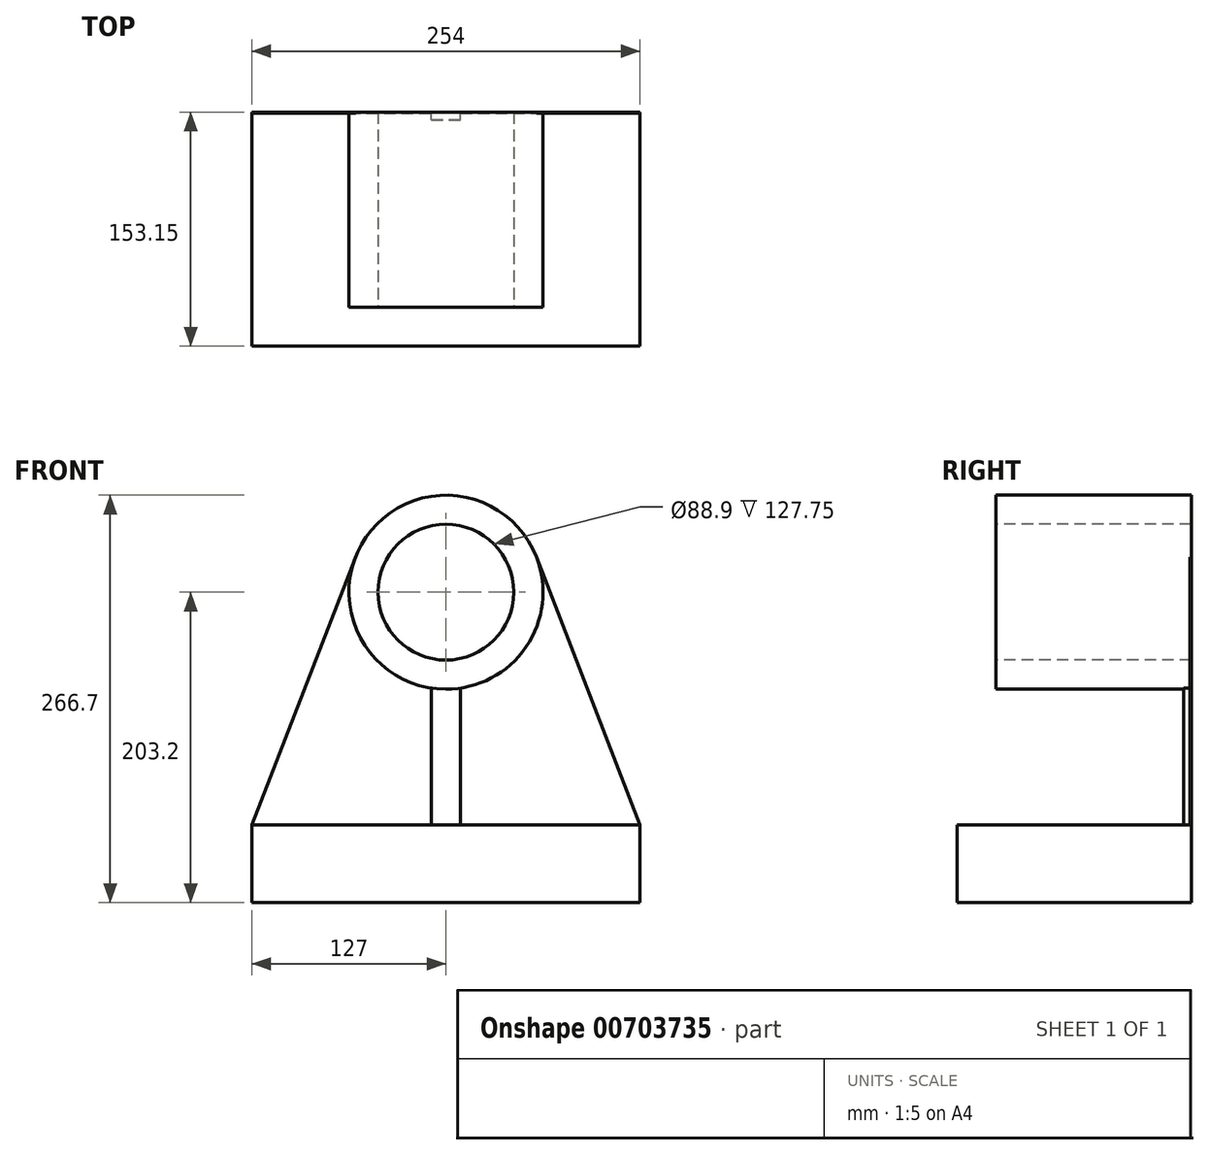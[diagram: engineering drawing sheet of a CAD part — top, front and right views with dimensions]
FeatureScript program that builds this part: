
annotation { "Feature Type Name" : "Feature", "Feature Type Description" : "" }
export const myFeature = defineFeature(function(context is Context, id is Id, definition is map)
    precondition{}
    {
        {
            assignVariable(context, id + "F0", {"name" : "C", "anyValue" : 0.75});
        }
        {
            var Q0;
            Q0=qCreatedBy(makeId("Front.planeOp"),FACE);
            var sketch = newSketch(context, id + "F1", { "sketchPlane" : qUnion([Q0])});
            skLineSegment(sketch, "E0.bottom", {"start": v(0, 0) * mm, "end": v(-254, 0) * mm});
            skLineSegment(sketch, "E0.left", {"start": v(0, 0) * mm, "end": v(0, 50.8) * mm});
            skLineSegment(sketch, "E0.right", {"start": v(-254, 0) * mm, "end": v(-254, 50.8) * mm});
            skLineSegment(sketch, "E1", {"start": v(0, 50.8) * mm, "end": v(-67.77, 226.1) * mm});
            skArc(sketch, "E2", {"start": v(-67.77, 226.1) * mm, "mid": v(-127, 266.7) * mm, "end": v(-186.23, 226.1) * mm});
            skLineSegment(sketch, "E3", {"start": v(-254, 50.8) * mm, "end": v(-186.23, 226.1) * mm});
            skLineSegment(sketch, "E4", {"start": v(-127, 203.2) * mm, "end": v(-127, 0) * mm, "construction": true});
            skSolve(sketch);
        }
        {
            var Q0;
            Q0 = qSketchRegion(id + "F1", true);
            extrude(context, id + "F2", {"entities" : qUnion([Q0]), "depth" : (getVariable(context, 'C')) * mm, "offsetDistance" : 25.4 * mm});
        }
        {
            var Q0;
            Q0=makeQuery(id+"F2.opExtrude","CAP_FACE",FACE,{"disambiguationData":[OSD([sQuery(id+"F1.wireOp",EDGE,"E0.bottom"),sQuery(id+"F1.wireOp",EDGE,"E0.left"),sQuery(id+"F1.wireOp",EDGE,"E0.right"),sQuery(id+"F1.wireOp",EDGE,"E1"),sQuery(id+"F1.wireOp",EDGE,"E2"),sQuery(id+"F1.wireOp",EDGE,"E3")])],"isStart":false});
            var sketch = newSketch(context, id + "F3", { "sketchPlane" : qUnion([Q0])});
            skLineSegment(sketch, "E5.bottom", {"start": v(0, 0) * mm, "end": v(-254, 0) * mm});
            skLineSegment(sketch, "E5.top", {"start": v(0, 50.8) * mm, "end": v(-254, 50.8) * mm});
            skLineSegment(sketch, "E5.left", {"start": v(0, 0) * mm, "end": v(0, 50.8) * mm});
            skLineSegment(sketch, "E5.right", {"start": v(-254, 0) * mm, "end": v(-254, 50.8) * mm});
            skSolve(sketch);
        }
        {
            var Q0;
            Q0 = qSketchRegion(id + "F3", true);
            extrude(context, id + "F4", {"entities" : qUnion([Q0]), "operationType" : NewBodyOperationType.ADD, "depth" : 152.4 * mm, "offsetDistance" : 25.4 * mm});
        }
        {
            var Q0;
            Q0=makeQuery(id+"F2.opExtrude","CAP_FACE",FACE,{"disambiguationData":[OSD([sQuery(id+"F1.wireOp",EDGE,"E0.bottom"),sQuery(id+"F1.wireOp",EDGE,"E0.left"),sQuery(id+"F1.wireOp",EDGE,"E0.right"),sQuery(id+"F1.wireOp",EDGE,"E1"),sQuery(id+"F1.wireOp",EDGE,"E2"),sQuery(id+"F1.wireOp",EDGE,"E3")])],"isStart":false});
            var sketch = newSketch(context, id + "F5", { "sketchPlane" : qUnion([Q0])});
            skLineSegment(sketch, "E6", {"start": v(-127, 50.8) * mm, "end": v(-127, 203.2) * mm, "construction": true});
            skLineSegment(sketch, "E7.bottom", {"start": v(-136.52, 50.8) * mm, "end": v(-117.47, 50.8) * mm});
            skLineSegment(sketch, "E7.top", {"start": v(-136.52, 203.2) * mm, "end": v(-117.47, 203.2) * mm});
            skLineSegment(sketch, "E7.left", {"start": v(-136.52, 50.8) * mm, "end": v(-136.52, 203.2) * mm});
            skLineSegment(sketch, "E7.right", {"start": v(-117.47, 50.8) * mm, "end": v(-117.47, 203.2) * mm});
            skSolve(sketch);
        }
        {
            var Q0;
            Q0 = qSketchRegion(id + "F5", true);
            extrude(context, id + "F6", {"entities" : qUnion([Q0]), "operationType" : NewBodyOperationType.ADD, "depth" : (5 - getVariable(context, 'C')) * mm, "offsetDistance" : 25.4 * mm});
        }
        {
            var Q0;
            Q0=makeQuery(id+"F2.opExtrude","CAP_FACE",FACE,{"disambiguationData":[OSD([sQuery(id+"F1.wireOp",EDGE,"E0.bottom"),sQuery(id+"F1.wireOp",EDGE,"E0.left"),sQuery(id+"F1.wireOp",EDGE,"E0.right"),sQuery(id+"F1.wireOp",EDGE,"E1"),sQuery(id+"F1.wireOp",EDGE,"E2"),sQuery(id+"F1.wireOp",EDGE,"E3")])],"isStart":false});
            var sketch = newSketch(context, id + "F7", { "sketchPlane" : qUnion([Q0])});
            skCircle(sketch, "E8", {"center": v(-127, 203.2) * mm, "radius": 63.5 * mm});
            skSolve(sketch);
        }
        {
            var Q0;
            Q0 = qSketchRegion(id + "F7", true);
            extrude(context, id + "F8", {"entities" : qUnion([Q0]), "operationType" : NewBodyOperationType.ADD, "depth" : 127 * mm, "offsetDistance" : 25.4 * mm});
        }
        {
            var Q0;
            Q0=makeQuery(id+"F8.opExtrude","CAP_FACE",FACE,{"disambiguationData":[OSD([sQuery(id+"F7.wireOp",EDGE,"E8")])],"isStart":false});
            var sketch = newSketch(context, id + "F9", { "sketchPlane" : qUnion([Q0])});
            skCircle(sketch, "E9", {"center": v(-127, 203.2) * mm, "radius": 44.45 * mm});
            skLineSegment(sketch, "E10", {"start": v(-127, 247.65) * mm, "end": v(-127, 266.7) * mm, "construction": true});
            skSolve(sketch);
        }
        {
            var Q0;
            Q0=makeQuery(id+"F9.imprint","IMPRINT",FACE,{"disambiguationData":[TD([[makeQuery(id+"F9.imprint","IMPRINT",EDGE,{"derivedFrom":sQuery(id+"F9.wireOp",EDGE,"E9")}),1.0]])]});
            extrude(context, id + "F10", {"entities" : qUnion([Q0]), "operationType" : NewBodyOperationType.REMOVE, "endBound" : BoundingType.THROUGH_ALL, "oppositeDirection" : true, "depth" : 25.4 * mm, "offsetDistance" : 25.4 * mm});
        }
    });
